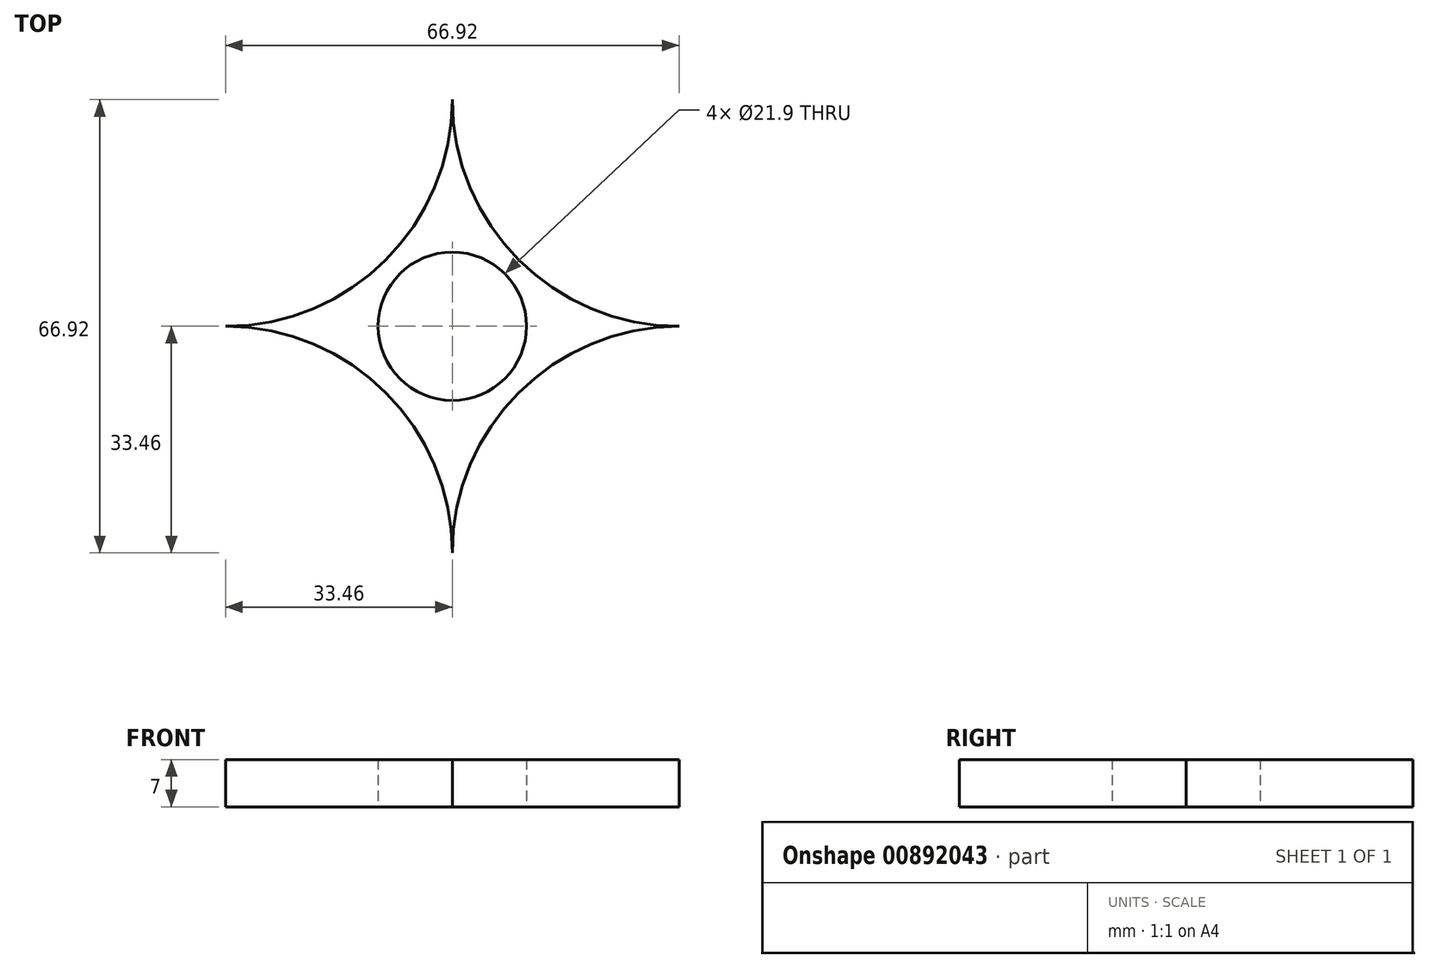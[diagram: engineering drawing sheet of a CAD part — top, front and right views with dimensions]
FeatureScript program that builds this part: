
annotation { "Feature Type Name" : "Feature", "Feature Type Description" : "" }
export const myFeature = defineFeature(function(context is Context, id is Id, definition is map)
    precondition{}
    {
        {
            var Q0;
            Q0=qCreatedBy(makeId("Top.planeOp"),FACE);
            var sketch = newSketch(context, id + "F0", { "sketchPlane" : qUnion([Q0])});
            skLineSegment(sketch, "E0", {"start": v(0, 0) * mm, "end": v(0, 33.46) * mm});
            skLineSegment(sketch, "E1", {"start": v(0, 33.46) * mm, "end": v(0, 0) * mm});
            skLineSegment(sketch, "E2", {"start": v(0, 0) * mm, "end": v(0, -33.46) * mm});
            skLineSegment(sketch, "E3", {"start": v(0, -33.46) * mm, "end": v(0, 0) * mm});
            skLineSegment(sketch, "E4", {"start": v(-33.46, 0) * mm, "end": v(0, 0) * mm});
            skLineSegment(sketch, "E5", {"start": v(33.46, 0) * mm, "end": v(0, 0) * mm});
            skArc(sketch, "E6", {"start": v(-33.46, 0) * mm, "mid": v(-9.8, 9.8) * mm, "end": v(0, 33.46) * mm});
            skArc(sketch, "E7", {"start": v(0, -33.46) * mm, "mid": v(-9.8, -9.8) * mm, "end": v(-33.46, 0) * mm});
            skArc(sketch, "E8", {"start": v(33.46, 0) * mm, "mid": v(9.8, -9.8) * mm, "end": v(0, -33.46) * mm});
            skArc(sketch, "E9", {"start": v(0, 33.46) * mm, "mid": v(9.8, 9.8) * mm, "end": v(33.46, 0) * mm});
            skCircle(sketch, "E10", {"center": v(0, 0) * mm, "radius": 10.95 * mm});
            skSolve(sketch);
        }
        {
            var Q0;
            {var subQ0=sQuery(id+"F0.wireOp",EDGE,"E7");Q0=makeQuery(id+"F0.imprint","IMPRINT",FACE,{"disambiguationData":[TD([[makeQuery(id+"F0.imprint","IMPRINT",EDGE,{"derivedFrom":subQ0}),-1.0]])]});}
            var Q1;
            {var subQ0=sQuery(id+"F0.wireOp",EDGE,"E6");Q1=makeQuery(id+"F0.imprint","IMPRINT",FACE,{"disambiguationData":[TD([[makeQuery(id+"F0.imprint","IMPRINT",EDGE,{"derivedFrom":subQ0}),-1.0]])]});}
            var Q2;
            {var subQ0=sQuery(id+"F0.wireOp",EDGE,"E9");Q2=makeQuery(id+"F0.imprint","IMPRINT",FACE,{"disambiguationData":[TD([[makeQuery(id+"F0.imprint","IMPRINT",EDGE,{"derivedFrom":subQ0}),-1.0]])]});}
            var Q3;
            {var subQ0=sQuery(id+"F0.wireOp",EDGE,"E8");Q3=makeQuery(id+"F0.imprint","IMPRINT",FACE,{"disambiguationData":[TD([[makeQuery(id+"F0.imprint","IMPRINT",EDGE,{"derivedFrom":subQ0}),-1.0]])]});}
            extrude(context, id + "F1", {"entities" : qUnion([Q0, Q1, Q2, Q3]), "depth" : 7 * mm, "offsetDistance" : 25 * mm});
        }
    });
